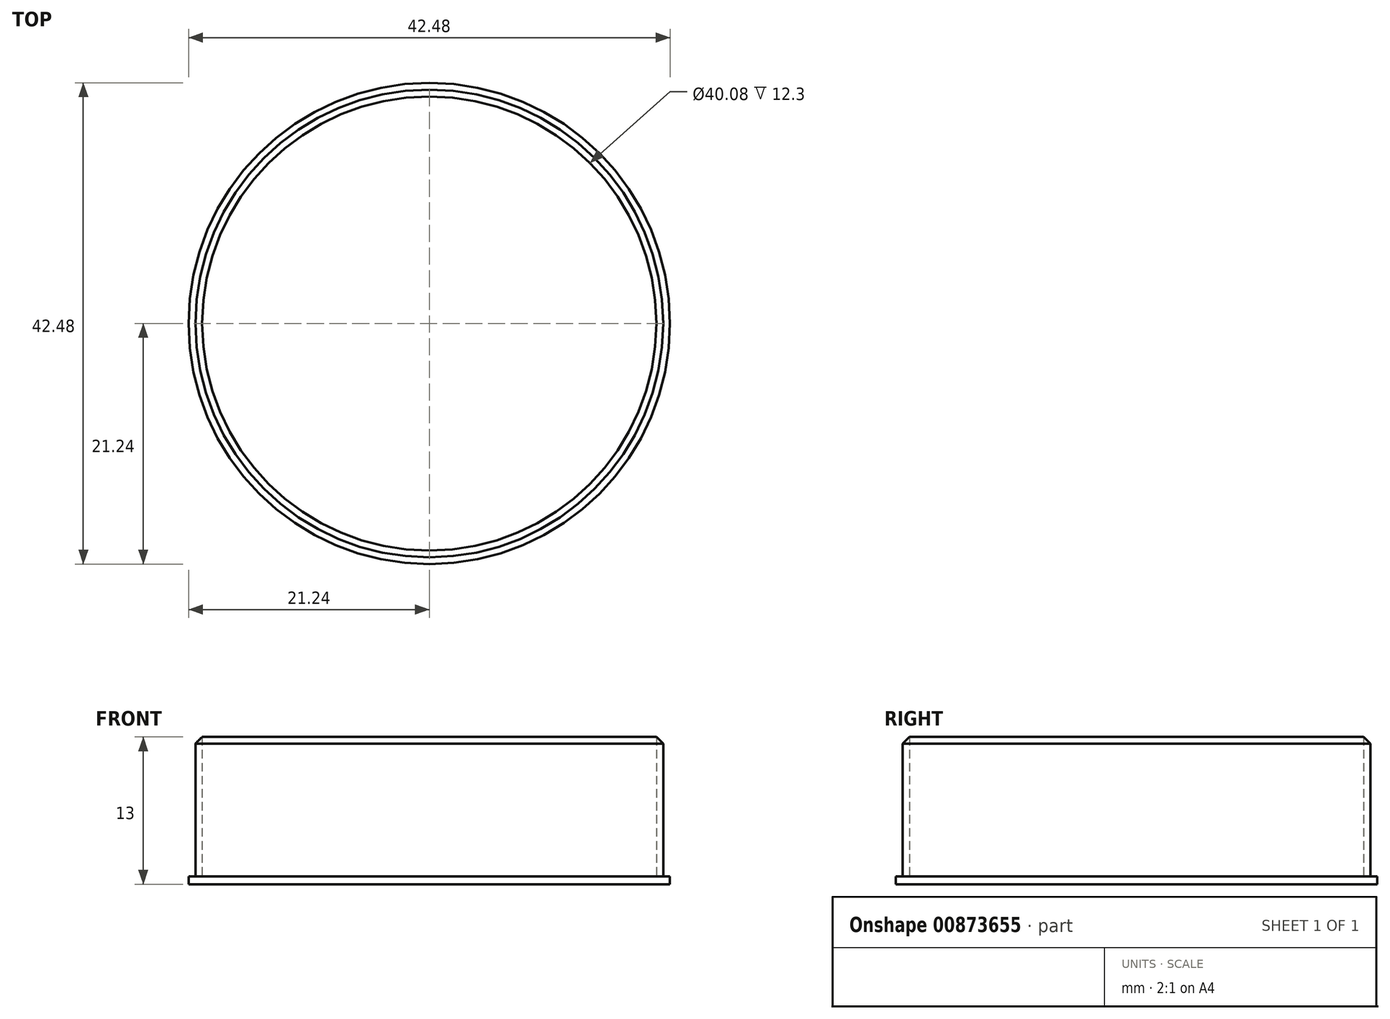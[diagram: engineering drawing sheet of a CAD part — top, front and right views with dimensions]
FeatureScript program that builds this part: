
annotation { "Feature Type Name" : "Feature", "Feature Type Description" : "" }
export const myFeature = defineFeature(function(context is Context, id is Id, definition is map)
    precondition{}
    {
        {
            var Q0;
            Q0=qCreatedBy(makeId("Top.planeOp"),FACE);
            var sketch = newSketch(context, id + "F0", { "sketchPlane" : qUnion([Q0])});
            skCircle(sketch, "E0", {"center": v(0, 0) * mm, "radius": 20.64 * mm});
            skCircle(sketch, "E1", {"center": v(0, 0) * mm, "radius": 20.04 * mm});
            skSolve(sketch);
        }
        {
            var Q0;
            Q0=makeQuery(id+"F0.imprint","IMPRINT",FACE,{"disambiguationData":[TD([[makeQuery(id+"F0.imprint","IMPRINT",EDGE,{"derivedFrom":sQuery(id+"F0.wireOp",EDGE,"E0")}),1.0]])]});
            extrude(context, id + "F1", {"entities" : qUnion([Q0]), "depth" : 12.7 * mm, "offsetDistance" : 25.4 * mm});
        }
        {
            var Q0;
            Q0=qCreatedBy(makeId("Top.planeOp"),FACE);
            var sketch = newSketch(context, id + "F2", { "sketchPlane" : qUnion([Q0])});
            skCircle(sketch, "E2", {"center": v(0, 0) * mm, "radius": 21.24 * mm});
            skSolve(sketch);
        }
        {
            var Q0;
            Q0=makeQuery(id+"F2.imprint","IMPRINT",FACE,{"disambiguationData":[TD([[makeQuery(id+"F2.imprint","IMPRINT",EDGE,{"derivedFrom":sQuery(id+"F2.wireOp",EDGE,"E2")}),1.0]])]});
            extrude(context, id + "F3", {"entities" : qUnion([Q0]), "operationType" : NewBodyOperationType.ADD, "oppositeDirection" : true, "depth" : .7 * mm, "offsetDistance" : 25.4 * mm});
        }
        {
            var Q0;
            Q0=makeQuery(id+"F1.opExtrude","CAP_EDGE",EDGE,{"disambiguationData":[OSD([sQuery(id+"F0.wireOp",EDGE,"E0")])],"isStart":false});
            chamfer(context, id + "F4", {"entities" : qUnion([Q0]), "chamferType" : ChamferType.OFFSET_ANGLE, "width" : 1 * mm, "oppositeDirection" : false, "angle" : 45 * degree, "tangentPropagation" : true});
        }
    });
